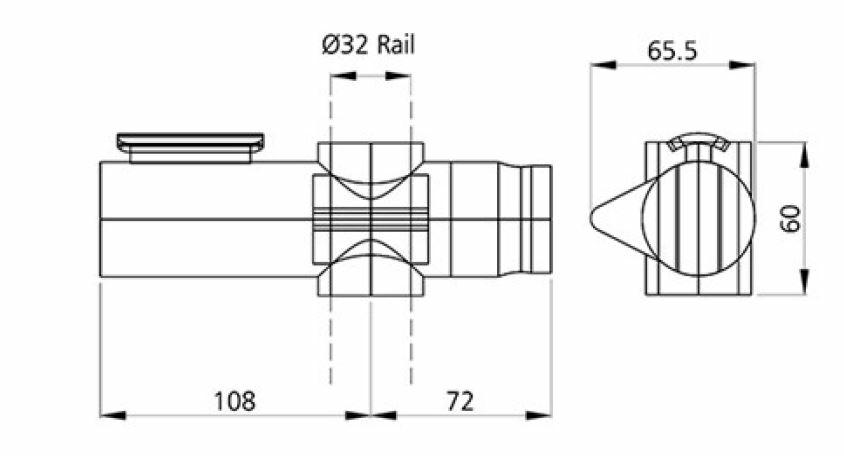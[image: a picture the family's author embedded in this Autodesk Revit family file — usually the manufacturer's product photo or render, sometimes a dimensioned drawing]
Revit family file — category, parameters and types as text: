
# Revit family: rba-bim-rba4604-068-RH
name_source: partatom
category: Plumbing Fixtures
revit_build: Autodesk Revit 2018 (Build: 20170223_1515(x64)
units: mm (PartAtom-declared; Revit-internal decimal feet)

## family parameters
Always vertical = Yes
Cut with Voids When Loaded = No
Part Type = Normal
Room Calculation Point = No
Round Connector Dimension = Use Diameter
Shared = No
Work Plane-Based = No

## types (3) — shared parameters
CW Connection = Yes
Distance Away from Toilet (default) = 1090 mm  [stored 3.57612 ft]
Distance Away from Wall (default) = 100 mm  [stored 0.328084 ft]
HW Connection = Yes
Manufacturer = RBA Group
OFFSET = 1000 mm  [stored 3.28084 ft]
Vent Connection = Yes
Waste Connection = Yes

## per-type parameters (varying)
| type | Description | Materials and Finishes | Modified Issue | URL |
| RBA4601-061 | Raffaello Shower T-Rail | Stainless Steel / White Antibacterial Finish | 20180813.01 | http://www.rba.com.au |
| RBA4604-068-RH | Raffaello Shower T-Rail & 4 Star Shower Set, RH | Stainless Steel / Matte Black Antibacterial Finish | 20200519.01 | www.rba.com.au |
| RBA4601-069 | Raffaello Shower T-Rail | Stainless Steel / Chrome Finish | 20180813.01 | http://www.rba.com.au |

note: column(s) folded — value = type name in every type: Model

note: [stored X ft] marks values corroborated as IEEE doubles in the binary element streams (Revit-internal decimal feet)

## geometry (parser evidence)
native form markers: Blend x8, Sweep x18
no freeform markers — native parametric forms only
